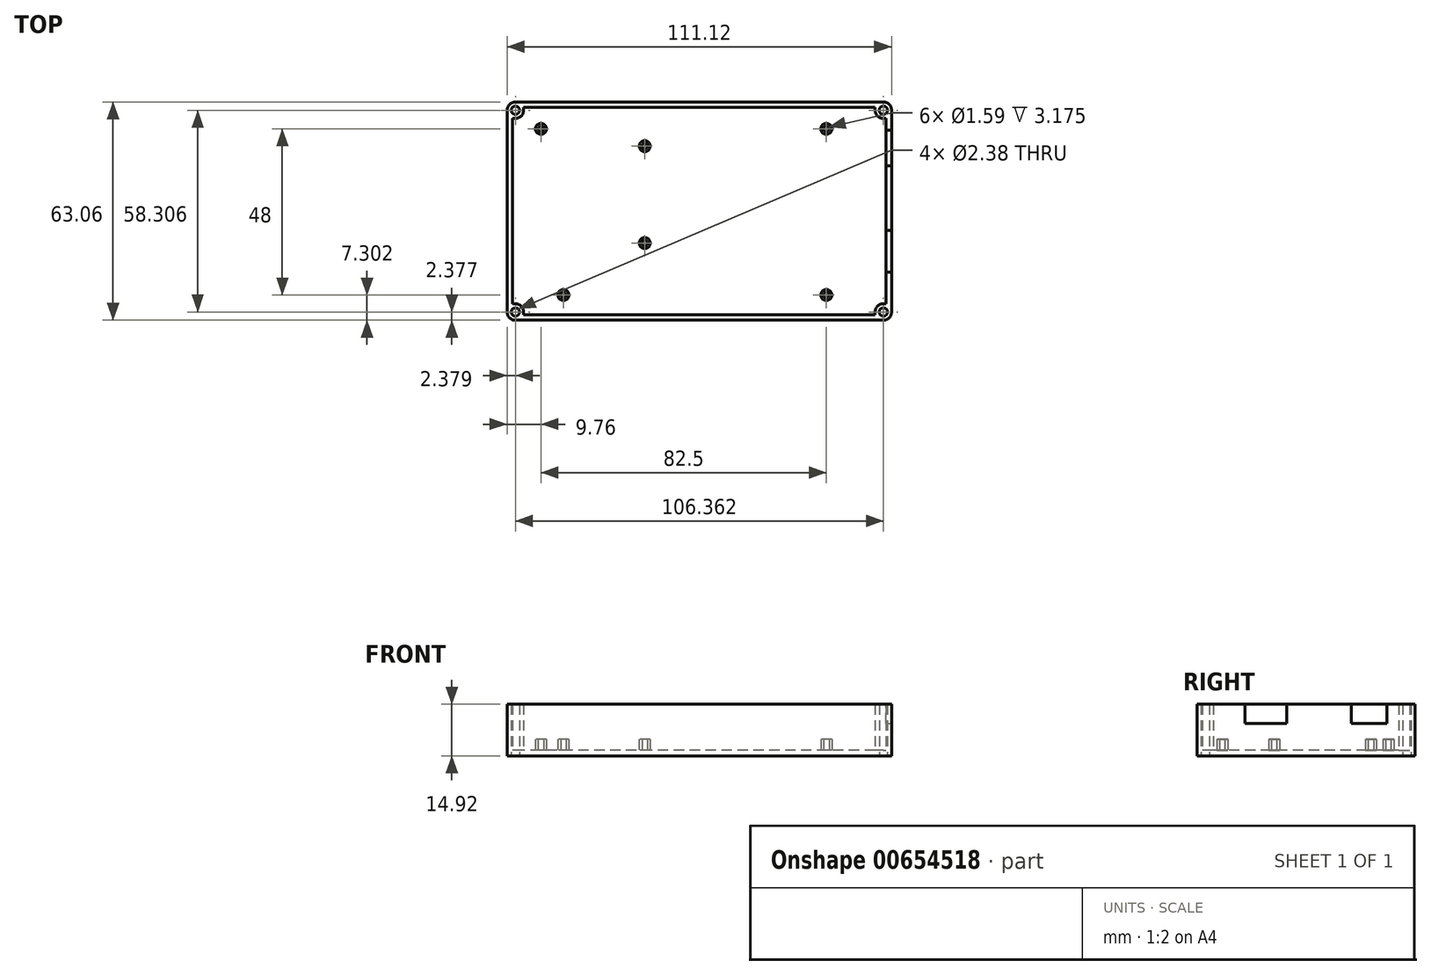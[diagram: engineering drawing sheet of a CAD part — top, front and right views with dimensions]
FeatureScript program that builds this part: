
annotation { "Feature Type Name" : "Feature", "Feature Type Description" : "" }
export const myFeature = defineFeature(function(context is Context, id is Id, definition is map)
    precondition{}
    {
        {
            var Q0;
            Q0=qCreatedBy(makeId("Top.planeOp"),FACE);
            var sketch = newSketch(context, id + "F0", { "sketchPlane" : qUnion([Q0])});
            skLineSegment(sketch, "E0.bottom", {"start": v(50.8, 26.77) * mm, "end": v(-50.8, 26.77) * mm});
            skLineSegment(sketch, "E0.top", {"start": v(50.8, -26.77) * mm, "end": v(-50.8, -26.77) * mm});
            skLineSegment(sketch, "E0.left", {"start": v(50.8, 26.77) * mm, "end": v(50.8, -26.77) * mm});
            skLineSegment(sketch, "E0.right", {"start": v(-50.8, 26.77) * mm, "end": v(-50.8, -26.77) * mm});
            skPoint(sketch, "E0.middle", {"position": v(0, 0) * mm});
            skSolve(sketch);
        }
        {
            var Q0;
            Q0=qCreatedBy(makeId("Top.planeOp"),FACE);
            var sketch = newSketch(context, id + "F1", { "sketchPlane" : qUnion([Q0])});
            skLineSegment(sketch, "E1.bottom", {"start": v(55.56, 31.53) * mm, "end": v(-55.56, 31.53) * mm});
            skLineSegment(sketch, "E1.top", {"start": v(55.56, -31.53) * mm, "end": v(-55.56, -31.53) * mm});
            skLineSegment(sketch, "E1.left", {"start": v(55.56, 31.53) * mm, "end": v(55.56, -31.53) * mm});
            skLineSegment(sketch, "E1.right", {"start": v(-55.56, 31.53) * mm, "end": v(-55.56, -31.53) * mm});
            skPoint(sketch, "E1.middle", {"position": v(0, 0) * mm});
            skLineSegment(sketch, "E2.bottom", {"start": v(53.97, 29.95) * mm, "end": v(-53.98, 29.95) * mm, "construction": true});
            skLineSegment(sketch, "E2.top", {"start": v(53.98, -29.95) * mm, "end": v(-53.97, -29.95) * mm, "construction": true});
            skLineSegment(sketch, "E2.left", {"start": v(53.97, 29.95) * mm, "end": v(53.98, -29.95) * mm, "construction": true});
            skLineSegment(sketch, "E2.right", {"start": v(-53.98, 29.95) * mm, "end": v(-53.97, -29.95) * mm, "construction": true});
            skSolve(sketch);
        }
        {
            var Q0;
            Q0=makeQuery(id+"F1.imprint","IMPRINT",FACE,{"disambiguationData":[TD([[makeQuery(id+"F1.imprint","IMPRINT",EDGE,{"derivedFrom":sQuery(id+"F1.wireOp",EDGE,"E1.bottom")}),1.0]])]});
            extrude(context, id + "F2", {"entities" : qUnion([Q0]), "depth" : 1.59 * mm, "offsetDistance" : 25.4 * mm});
        }
        {
            var Q0;
            Q0=makeQuery(id+"F2.opExtrude","CAP_FACE",FACE,{"disambiguationData":[OSD([sQuery(id+"F1.wireOp",EDGE,"E1.bottom"),sQuery(id+"F1.wireOp",EDGE,"E1.top"),sQuery(id+"F1.wireOp",EDGE,"E1.left"),sQuery(id+"F1.wireOp",EDGE,"E1.right")])],"isStart":false});
            var sketch = newSketch(context, id + "F3", { "sketchPlane" : qUnion([Q0])});
            skLineSegment(sketch, "E3.bottom", {"start": v(55.56, 31.53) * mm, "end": v(-55.56, 31.53) * mm});
            skLineSegment(sketch, "E3.top", {"start": v(55.56, -31.53) * mm, "end": v(-55.56, -31.53) * mm});
            skLineSegment(sketch, "E3.left", {"start": v(55.56, 31.53) * mm, "end": v(55.56, -31.53) * mm});
            skLineSegment(sketch, "E3.right", {"start": v(-55.56, 31.53) * mm, "end": v(-55.56, -31.53) * mm});
            skPoint(sketch, "E3.middle", {"position": v(0, 0) * mm});
            skLineSegment(sketch, "E4.left", {"start": v(53.97, 26.77) * mm, "end": v(53.97, -26.77) * mm});
            skLineSegment(sketch, "E4.right", {"start": v(-53.97, 26.77) * mm, "end": v(-53.97, -26.77) * mm});
            skArc(sketch, "E5", {"start": v(-53.18, 26.77) * mm, "mid": v(-51.5, 27.47) * mm, "end": v(-50.8, 29.15) * mm});
            skCircle(sketch, "E6", {"center": v(-53.18, 29.15) * mm, "radius": 1.2 * mm});
            skLineSegment(sketch, "E7", {"start": v(-50.8, 29.15) * mm, "end": v(-50.8, 29.95) * mm});
            skLineSegment(sketch, "E8", {"start": v(-53.18, 26.77) * mm, "end": v(-53.97, 26.77) * mm});
            skLineSegment(sketch, "E9", {"start": v(-55.56, 31.53) * mm, "end": v(-51.5, 27.47) * mm, "construction": true});
            skPoint(sketch, "E10", {"position": v(-53.53, 29.5) * mm});
            skPoint(sketch, "E11.orphan", {"position": v(-53.97, 37.1) * mm});
            skCircle(sketch, "E12.MirrorC", {"center": v(-53.18, -29.15) * mm, "radius": 1.2 * mm});
            skLineSegment(sketch, "E13.MirrorCS", {"start": v(-53.18, -26.77) * mm, "end": v(-53.97, -26.77) * mm});
            skArc(sketch, "E14.MirrorCS", {"start": v(-53.18, -26.77) * mm, "mid": v(-51.5, -27.47) * mm, "end": v(-50.8, -29.15) * mm});
            skLineSegment(sketch, "E15.MirrorCS", {"start": v(-50.8, -29.15) * mm, "end": v(-50.8, -29.95) * mm});
            skCircle(sketch, "E16.MirrorC", {"center": v(53.18, 29.15) * mm, "radius": 1.2 * mm});
            skLineSegment(sketch, "E17.MirrorCS", {"start": v(50.8, 29.15) * mm, "end": v(50.8, 29.95) * mm});
            skArc(sketch, "E18.MirrorCS", {"start": v(53.18, 26.77) * mm, "mid": v(51.5, 27.47) * mm, "end": v(50.8, 29.15) * mm});
            skLineSegment(sketch, "E19.MirrorCS", {"start": v(53.18, 26.77) * mm, "end": v(53.97, 26.77) * mm});
            skCircle(sketch, "E20.MirrorC", {"center": v(53.18, -29.15) * mm, "radius": 1.2 * mm});
            skLineSegment(sketch, "E21.MirrorCS", {"start": v(53.18, -26.77) * mm, "end": v(53.97, -26.77) * mm});
            skArc(sketch, "E22.MirrorCS", {"start": v(53.18, -26.77) * mm, "mid": v(51.5, -27.47) * mm, "end": v(50.8, -29.15) * mm});
            skLineSegment(sketch, "E23.MirrorCS", {"start": v(50.8, -29.15) * mm, "end": v(50.8, -29.95) * mm});
            skPoint(sketch, "E24.orphan", {"position": v(-53.97, -36.92) * mm});
            skLineSegment(sketch, "E25.trimOffspring", {"start": v(50.8, -29.95) * mm, "end": v(-50.8, -29.95) * mm});
            skPoint(sketch, "E26.orphan", {"position": v(53.97, -37.1) * mm});
            skLineSegment(sketch, "E27.trimOffspring", {"start": v(50.8, 29.95) * mm, "end": v(-50.8, 29.95) * mm});
            skPoint(sketch, "E28.orphan", {"position": v(53.97, 36.92) * mm});
            skSolve(sketch);
        }
        {
            var Q0;
            Q0 = qSketchRegion(id + "F3", true);
            extrude(context, id + "F4", {"entities" : qUnion([Q0]), "operationType" : NewBodyOperationType.ADD, "depth" : 13.33 * mm, "offsetDistance" : 25.4 * mm});
        }
        {
            var Q0;
            Q0=makeQuery(id+"F4.boolean.opBoolean","MERGE",EDGE,{"derivedFrom":[makeQuery(id+"F2.opExtrude","SWEPT_EDGE",EDGE,{"disambiguationData":[OSD([sQuery(id+"F1.wireOp",EDGE,"E1.top"),sQuery(id+"F1.wireOp",EDGE,"E1.left")])]}),makeQuery(id+"F4.opExtrude","SWEPT_EDGE",EDGE,{"disambiguationData":[OSD([sQuery(id+"F3.wireOp",EDGE,"E3.top"),sQuery(id+"F3.wireOp",EDGE,"E3.left")])]})]});
            var Q1;
            Q1=makeQuery(id+"F4.boolean.opBoolean","MERGE",EDGE,{"derivedFrom":[makeQuery(id+"F2.opExtrude","SWEPT_EDGE",EDGE,{"disambiguationData":[OSD([sQuery(id+"F1.wireOp",EDGE,"E1.bottom"),sQuery(id+"F1.wireOp",EDGE,"E1.left")])]}),makeQuery(id+"F4.opExtrude","SWEPT_EDGE",EDGE,{"disambiguationData":[OSD([sQuery(id+"F3.wireOp",EDGE,"E3.bottom"),sQuery(id+"F3.wireOp",EDGE,"E3.left")])]})]});
            var Q2;
            Q2=makeQuery(id+"F4.boolean.opBoolean","MERGE",EDGE,{"derivedFrom":[makeQuery(id+"F2.opExtrude","SWEPT_EDGE",EDGE,{"disambiguationData":[OSD([sQuery(id+"F1.wireOp",EDGE,"E1.top"),sQuery(id+"F1.wireOp",EDGE,"E1.right")])]}),makeQuery(id+"F4.opExtrude","SWEPT_EDGE",EDGE,{"disambiguationData":[OSD([sQuery(id+"F3.wireOp",EDGE,"E3.top"),sQuery(id+"F3.wireOp",EDGE,"E3.right")])]})]});
            var Q3;
            Q3=makeQuery(id+"F4.boolean.opBoolean","MERGE",EDGE,{"derivedFrom":[makeQuery(id+"F2.opExtrude","SWEPT_EDGE",EDGE,{"disambiguationData":[OSD([sQuery(id+"F1.wireOp",EDGE,"E1.bottom"),sQuery(id+"F1.wireOp",EDGE,"E1.right")])]}),makeQuery(id+"F4.opExtrude","SWEPT_EDGE",EDGE,{"disambiguationData":[OSD([sQuery(id+"F3.wireOp",EDGE,"E3.bottom"),sQuery(id+"F3.wireOp",EDGE,"E3.right")])]})]});
            fillet(context, id + "F5", {"entities" : qUnion([Q0, Q1, Q2, Q3]), "radius" : 2.38 * mm, "tangentPropagation" : true, "allowEdgeOverflow" : false});
        }
        {
            var Q0;
            Q0=makeQuery(id+"F4.boolean.opBoolean","MERGE",FACE,{"derivedFrom":[makeQuery(id+"F2.opExtrude","SWEPT_FACE",FACE,{"disambiguationData":[OSD([sQuery(id+"F1.wireOp",EDGE,"E1.left")])]}),makeQuery(id+"F4.opExtrude","SWEPT_FACE",FACE,{"disambiguationData":[OSD([sQuery(id+"F3.wireOp",EDGE,"E3.left")])]})]});
            var sketch = newSketch(context, id + "F6", { "sketchPlane" : qUnion([Q0])});
            skLineSegment(sketch, "E29.bottom", {"start": v(-17.59, 14.92) * mm, "end": v(-5.52, 14.92) * mm});
            skLineSegment(sketch, "E29.top", {"start": v(-17.59, 9.4) * mm, "end": v(-5.52, 9.4) * mm});
            skLineSegment(sketch, "E29.left", {"start": v(-17.59, 14.92) * mm, "end": v(-17.59, 9.4) * mm});
            skLineSegment(sketch, "E29.right", {"start": v(-5.52, 14.92) * mm, "end": v(-5.52, 9.4) * mm});
            skLineSegment(sketch, "E30.bottom", {"start": v(13.14, 14.92) * mm, "end": v(23.43, 14.92) * mm});
            skLineSegment(sketch, "E30.top", {"start": v(13.14, 9.4) * mm, "end": v(23.43, 9.4) * mm});
            skLineSegment(sketch, "E30.left", {"start": v(13.14, 14.92) * mm, "end": v(13.14, 9.4) * mm});
            skLineSegment(sketch, "E30.right", {"start": v(23.43, 14.92) * mm, "end": v(23.43, 9.4) * mm});
            skPoint(sketch, "E31", {"position": v(-11.56, 9.4) * mm});
            skPoint(sketch, "E32", {"position": v(18.29, 9.4) * mm});
            skSolve(sketch);
        }
        {
            var Q0;
            Q0 = qSketchRegion(id + "F6", true);
            extrude(context, id + "F7", {"entities" : qUnion([Q0]), "operationType" : NewBodyOperationType.REMOVE, "endBound" : BoundingType.UP_TO_NEXT, "oppositeDirection" : true, "depth" : 25.4 * mm, "offsetDistance" : 25.4 * mm});
        }
        {
            var Q0;
            Q0=makeQuery(id+"F4.boolean.opBoolean","SPLIT",FACE,{"disambiguationData":[TD([makeQuery(id+"F4.opExtrude","SWEPT_FACE",FACE,{"disambiguationData":[OSD([sQuery(id+"F3.wireOp",EDGE,"E4.left")])]})])],"derivedFrom":makeQuery(id+"F2.opExtrude","CAP_FACE",FACE,{"disambiguationData":[OSD([sQuery(id+"F1.wireOp",EDGE,"E1.bottom"),sQuery(id+"F1.wireOp",EDGE,"E1.top"),sQuery(id+"F1.wireOp",EDGE,"E1.left"),sQuery(id+"F1.wireOp",EDGE,"E1.right")])],"isStart":false})});
            var sketch = newSketch(context, id + "F8", { "sketchPlane" : qUnion([Q0])});
            skCircle(sketch, "E33", {"center": v(-45.8, 23.77) * mm, "radius": 0.8 * mm});
            skCircle(sketch, "E34", {"center": v(-39.3, -24.23) * mm, "radius": 0.8 * mm});
            skCircle(sketch, "E35", {"center": v(-15.8, 18.77) * mm, "radius": 0.8 * mm});
            skCircle(sketch, "E36", {"center": v(-15.8, -9.23) * mm, "radius": 0.8 * mm});
            skCircle(sketch, "E37", {"center": v(36.7, 23.77) * mm, "radius": 0.8 * mm});
            skCircle(sketch, "E38", {"center": v(36.7, -24.23) * mm, "radius": 0.8 * mm});
            skCircle(sketch, "E39", {"center": v(-45.8, 23.77) * mm, "radius": 1.59 * mm});
            skCircle(sketch, "E40", {"center": v(-39.3, -24.23) * mm, "radius": 1.59 * mm});
            skCircle(sketch, "E41", {"center": v(-15.8, 18.77) * mm, "radius": 1.59 * mm});
            skCircle(sketch, "E42", {"center": v(-15.8, -9.23) * mm, "radius": 1.59 * mm});
            skCircle(sketch, "E43", {"center": v(36.7, 23.77) * mm, "radius": 1.59 * mm});
            skCircle(sketch, "E44", {"center": v(36.7, -24.23) * mm, "radius": 1.59 * mm});
            skSolve(sketch);
        }
        {
            var Q0;
            Q0 = qSketchRegion(id + "F8", true);
            extrude(context, id + "F9", {"entities" : qUnion([Q0]), "operationType" : NewBodyOperationType.ADD, "depth" : 3.17 * mm, "offsetDistance" : 25.4 * mm});
        }
        {
            var Q0;
            {var subQ0=sQuery(id+"F3.wireOp",EDGE,"E18.MirrorCS");var subQ1=sQuery(id+"F3.wireOp",EDGE,"E17.MirrorCS");var subQ2=sQuery(id+"F3.wireOp",EDGE,"E16.MirrorC");var subQ3=sQuery(id+"F3.wireOp",EDGE,"E15.MirrorCS");var subQ4=sQuery(id+"F3.wireOp",EDGE,"E14.MirrorCS");var subQ5=sQuery(id+"F3.wireOp",EDGE,"E13.MirrorCS");var subQ6=sQuery(id+"F3.wireOp",EDGE,"E12.MirrorC");var subQ7=sQuery(id+"F3.wireOp",EDGE,"E8");var subQ8=sQuery(id+"F3.wireOp",EDGE,"E7");var subQ9=sQuery(id+"F3.wireOp",EDGE,"E6");var subQ10=sQuery(id+"F3.wireOp",EDGE,"E5");var subQ11=sQuery(id+"F3.wireOp",EDGE,"E3.top");var subQ12=sQuery(id+"F3.wireOp",EDGE,"E3.left");var subQ13=sQuery(id+"F3.wireOp",EDGE,"E3.bottom");var subQ15=sQuery(id+"F1.wireOp",EDGE,"E1.bottom");var subQ17=sQuery(id+"F3.wireOp",EDGE,"E22.MirrorCS");var subQ19=sQuery(id+"F3.wireOp",EDGE,"E25.trimOffspring");var subQ20=sQuery(id+"F3.wireOp",EDGE,"E3.right");var subQ21=sQuery(id+"F3.wireOp",EDGE,"E19.MirrorCS");var subQ22=sQuery(id+"F3.wireOp",EDGE,"E23.MirrorCS");var subQ23=sQuery(id+"F3.wireOp",EDGE,"E4.left");var subQ24=sQuery(id+"F3.wireOp",EDGE,"E4.right");var subQ25=sQuery(id+"F3.wireOp",EDGE,"E20.MirrorC");var subQ26=sQuery(id+"F3.wireOp",EDGE,"E21.MirrorCS");var subQ27=sQuery(id+"F3.wireOp",EDGE,"E27.trimOffspring");Q0=makeQuery(id+"F7.boolean.opBoolean","SPLIT",FACE,{"disambiguationData":[TD([makeQuery(id+"F2.opExtrude","SWEPT_FACE",FACE,{"disambiguationData":[OSD([subQ15])]})])],"derivedFrom":makeQuery(id+"F4.opExtrude","CAP_FACE",FACE,{"disambiguationData":[OSD([subQ13,subQ11,subQ12,subQ20,subQ23,subQ24,subQ10,subQ9,subQ8,subQ7,subQ6,subQ5,subQ4,subQ3,subQ2,subQ1,subQ0,subQ21,subQ25,subQ26,subQ17,subQ22,subQ19,subQ27])],"isStart":false})});}
            var sketch = newSketch(context, id + "F10", { "sketchPlane" : qUnion([Q0])});
            skCircle(sketch, "E45.0", {"center": v(-53.18, 29.15) * mm, "radius": 1.2 * mm});
            skCircle(sketch, "E46.0", {"center": v(-53.18, -29.15) * mm, "radius": 1.2 * mm});
            skCircle(sketch, "E47.0", {"center": v(53.18, -29.15) * mm, "radius": 1.2 * mm});
            skCircle(sketch, "E48.0", {"center": v(53.18, 29.15) * mm, "radius": 1.2 * mm});
            skSolve(sketch);
        }
        {
            var Q0;
            Q0 = qSketchRegion(id + "F10", true);
            extrude(context, id + "F11", {"entities" : qUnion([Q0]), "operationType" : NewBodyOperationType.REMOVE, "endBound" : BoundingType.THROUGH_ALL, "oppositeDirection" : true, "depth" : 25.4 * mm, "offsetDistance" : 25.4 * mm});
        }
    });
